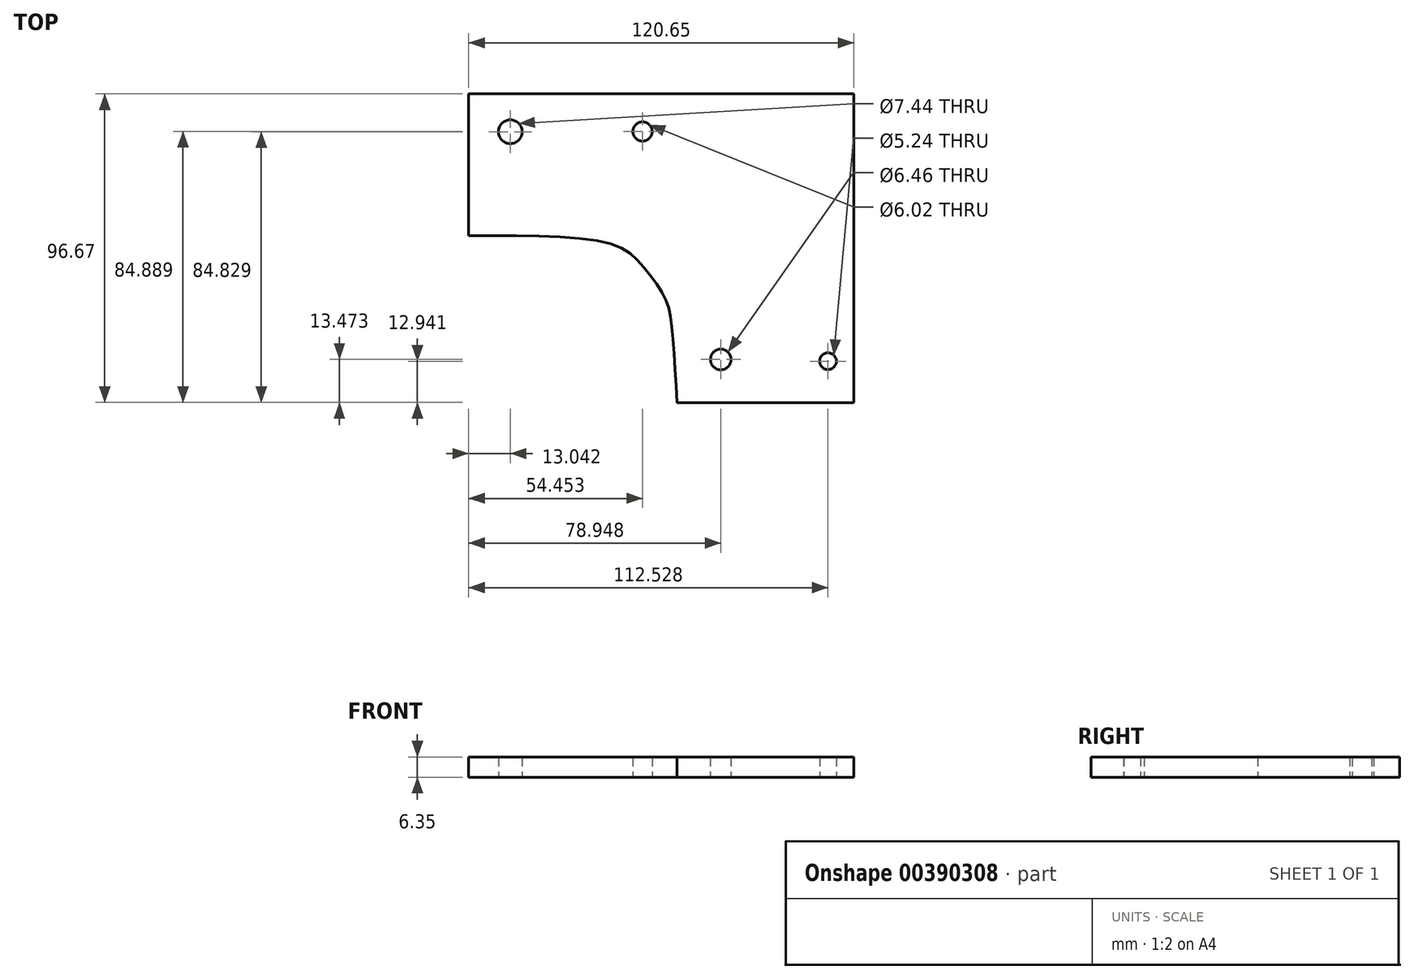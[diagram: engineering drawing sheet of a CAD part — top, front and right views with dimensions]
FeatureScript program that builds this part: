
annotation { "Feature Type Name" : "Feature", "Feature Type Description" : "" }
export const myFeature = defineFeature(function(context is Context, id is Id, definition is map)
    precondition{}
    {
        {
            var Q0;
            Q0=qCreatedBy(makeId("Top.planeOp"),FACE);
            var sketch = newSketch(context, id + "F0", { "sketchPlane" : qUnion([Q0])});
            skLineSegment(sketch, "E0", {"start": v(-70.3, 50.57) * mm, "end": v(50.35, 50.57) * mm});
            skLineSegment(sketch, "E1", {"start": v(50.35, 50.57) * mm, "end": v(50.35, -46.1) * mm});
            skLineSegment(sketch, "E2", {"start": v(50.35, -46.1) * mm, "end": v(-5.08, -46.1) * mm});
            skLineSegment(sketch, "E3", {"start": v(-70.3, 50.57) * mm, "end": v(-70.3, 6.14) * mm});
            skCircle(sketch, "E4", {"center": v(8.65, -32.63) * mm, "radius": 3.23 * mm});
            skCircle(sketch, "E5", {"center": v(42.23, -33.16) * mm, "radius": 2.62 * mm});
            skCircle(sketch, "E6", {"center": v(-57.26, 38.73) * mm, "radius": 3.72 * mm});
            skCircle(sketch, "E7", {"center": v(-15.85, 38.79) * mm, "radius": 3 * mm});
            skFitSpline(sketch, "E8", {"points": [v(-70.3, 6.14) * mm, v(-24.83, 3.3) * mm, v(-15.82, -3.3) * mm, v(-9.01, -12.92) * mm, v(-6.8, -21.13) * mm, v(-5.08, -46.1) * mm], "startDerivative": vector(173.98, 0.81) * mm, "endDerivative": vector(6.65, -122.7) * mm});
            skSolve(sketch);
        }
        {
            var Q0;
            Q0=makeQuery(id+"F0.imprint","IMPRINT",FACE,{"disambiguationData":[TD([[makeQuery(id+"F0.imprint","IMPRINT",EDGE,{"derivedFrom":sQuery(id+"F0.wireOp",EDGE,"E0")}),-1.0]])]});
            extrude(context, id + "F1", {"entities" : qUnion([Q0]), "depth" : 6.35 * mm});
        }
    });
